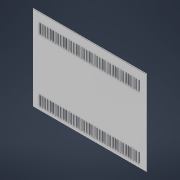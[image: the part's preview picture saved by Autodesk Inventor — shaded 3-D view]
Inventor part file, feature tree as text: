
AUTODESK INVENTOR PART (.ipt)
format: ipt  version: 2022 (Build 260153070, 153G)  size: 577,536 bytes
history: native  units: mm
features: chamfer x2, extrude x1, other x1, sketch x1
ambient origin geometry x8: Origin, YZ Plane, XZ Plane, XY Plane, X Axis, Y Axis, Z Axis, Center Point
bodies: Body1 (feature_tree)
feature tree (5):
  extrude  "Выдавливание2"  Depth=3.0mm
  chamfer  "Фаска1"  Distance=218.0mm
  chamfer  "Фаска2"  Distance=163.0mm
  other  "Определение главной стороны"
  sketch  "Эскиз2"
